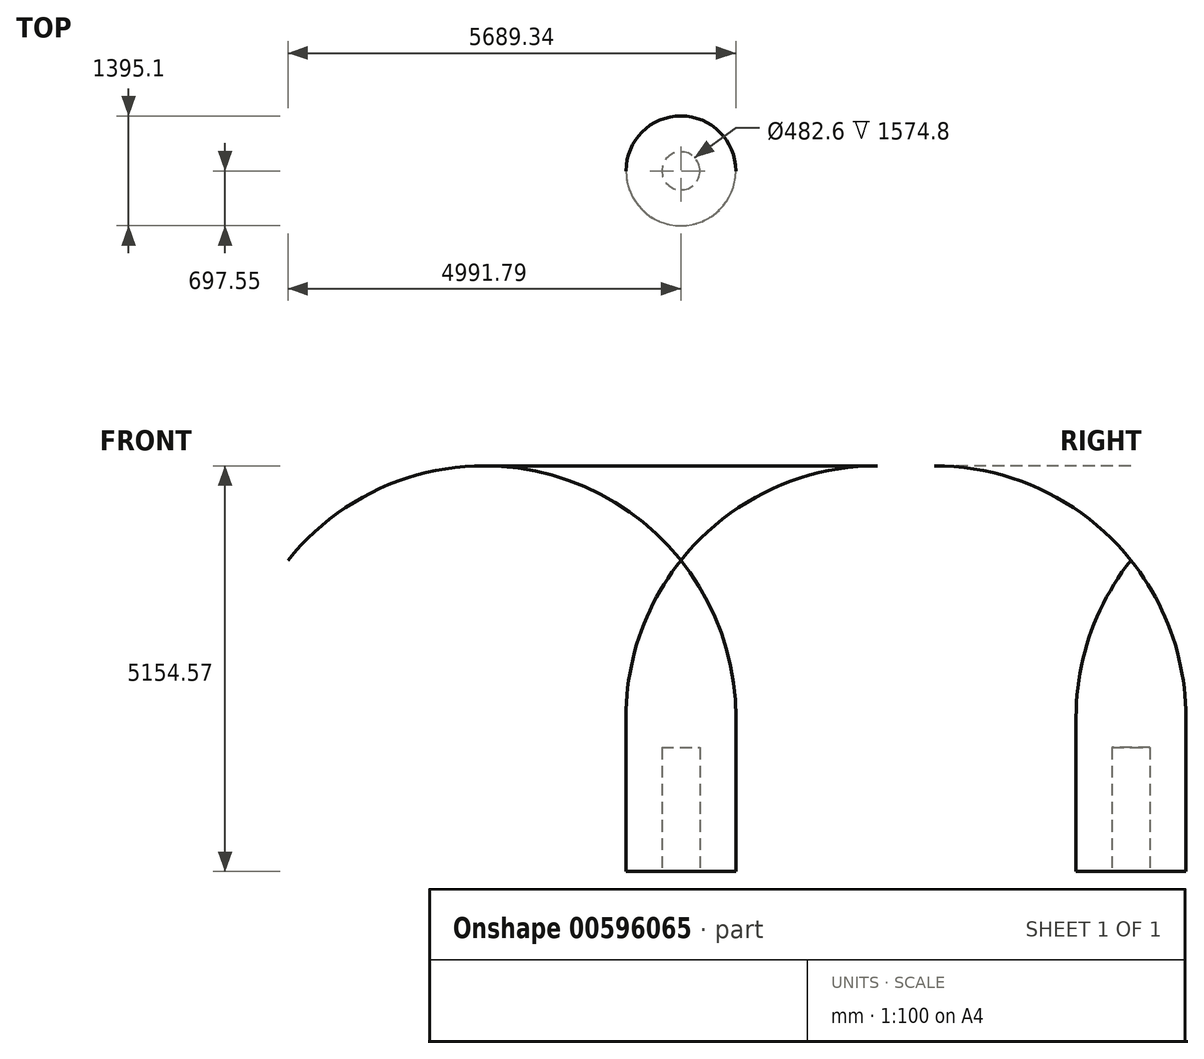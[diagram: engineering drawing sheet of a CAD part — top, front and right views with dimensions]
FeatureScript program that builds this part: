
annotation { "Feature Type Name" : "Feature", "Feature Type Description" : "" }
export const myFeature = defineFeature(function(context is Context, id is Id, definition is map)
    precondition{}
    {
        {
            var Q0;
            Q0=qCreatedBy(makeId("Right.planeOp"),FACE);
            var sketch = newSketch(context, id + "F0", { "sketchPlane" : qUnion([Q0])});
            skLineSegment(sketch, "E0.bottom", {"start": v(0, 0) * mm, "end": v(697.55, 0) * mm});
            skLineSegment(sketch, "E0.left", {"start": v(0, 0) * mm, "end": v(0, 1961.12) * mm});
            skLineSegment(sketch, "E0.right", {"start": v(697.55, 0) * mm, "end": v(697.55, 1961.12) * mm});
            skLineSegment(sketch, "E1", {"start": v(0, 1961.12) * mm, "end": v(0, 3953.26) * mm});
            skArc(sketch, "E2", {"start": v(697.55, 1961.12) * mm, "mid": v(518.12, 3016.49) * mm, "end": v(0, 3953.26) * mm});
            skLineSegment(sketch, "E3", {"start": v(0, 1574.8) * mm, "end": v(241.3, 1574.8) * mm});
            skLineSegment(sketch, "E4", {"start": v(241.3, 1574.8) * mm, "end": v(241.3, 0) * mm});
            skSolve(sketch);
        }
        {
            var Q0;
            {var subQ1=sQuery(id+"F0.wireOp",EDGE,"E0.right");Q0=makeQuery(id+"F0.imprint","IMPRINT",FACE,{"disambiguationData":[TD([[makeQuery(id+"F0.imprint","IMPRINT",EDGE,{"derivedFrom":subQ1}),1.0]])]});}
            var Q1;
            Q1=sQuery(id+"F0.wireOp",EDGE,"E1");
            revolve(context, id + "F1", {"entities" : qUnion([Q0]), "axis" : qUnion([Q1]), "revolveType" : RevolveType.FULL});
        }
    });
